# Revit family: Sink-Vessel-Lavatory-KOHLER-PARLIAMENT-K-14715T_1
name_source: partatom
category: Plumbing Fixtures
revit_build: Autodesk Revit 2017 (Build: 20160225_1515(x64)
units: mm (PartAtom-declared; Revit-internal decimal feet)

## family parameters
Cut with Voids When Loaded = No
Host = Face
OmniClass Number = 23.31.13.00
OmniClass Title = Sinks
Part Type = Normal
Room Calculation Point = No
Round Connector Dimension = Use Diameter
Shared = No

## types (6) — shared parameters
ADA Compliant = No
Assembly Code = D2010400
CW Connection = No
Cold Water Inlet = Cold Water Inlet
Date Modified = 08/24/2020
Default Elevation = 36"
Drain Included = No
Finish = Kohler-Vitreous_China-0-White
HW Connection = No
Height = 7 3/8"
Hot Water Inlet = Hot Water Inlet
Length = 22 3/16"
Manufacturer = KOHLER Co.
Master Format 2014 = 22 41 16
Master Format 2014 Name = Residential Lavatories and Sinks
Material = Vitreous china
Product Documentation Link = https://files.kohler.com.cn
Product Name = PARLIAMENT
Product Page URL = https://www.kohler.com.cn
URL = http://www.kohler.com.cn
Vent Connection = No
Waste Connection = Yes
Waste Water Outlet = Waste Water Outlet
WaterSense Certified = No
Width = 17 3/8"

## per-type parameters (varying)
| type | 4 Inch Faucet Hole | 8 Inch Faucet Hole | Description | Faucet Hole Spacing | Model | Type |
| Single Hole, 0-White | No | No | fashion washbasin | 0" | K-14715T-1-0 | 1 |
| Glazed Surface, Single Hole, 0-White | No | No | Semi-recessed basin | 0" | K-14715T-1G-0 | 2 |
| Glazed Surface, 4 Inch Faucet Hole, 0-White | Yes | No | Semi-recessed basin | 4" | K-14715T-4G-0 | 4 |
| 4 Inch Faucet Hole, 0-White | Yes | No | fashion washbasin | 4" | K-14715T-4-0 | 3 |
| Glazed Surface, 8 Inch Faucet Hole, 0-White | No | Yes | Semi-recessed basin | 8 1/16" | K-14715T-8G-0 | 6 |
| 8 Inch Faucet Hole, 0-White | No | Yes | fashion washbasin | 8 1/16" | K-14715T-8-0 | 5 |

## geometry (parser evidence)
native form markers: Sweep x4
no freeform markers — native parametric forms only
